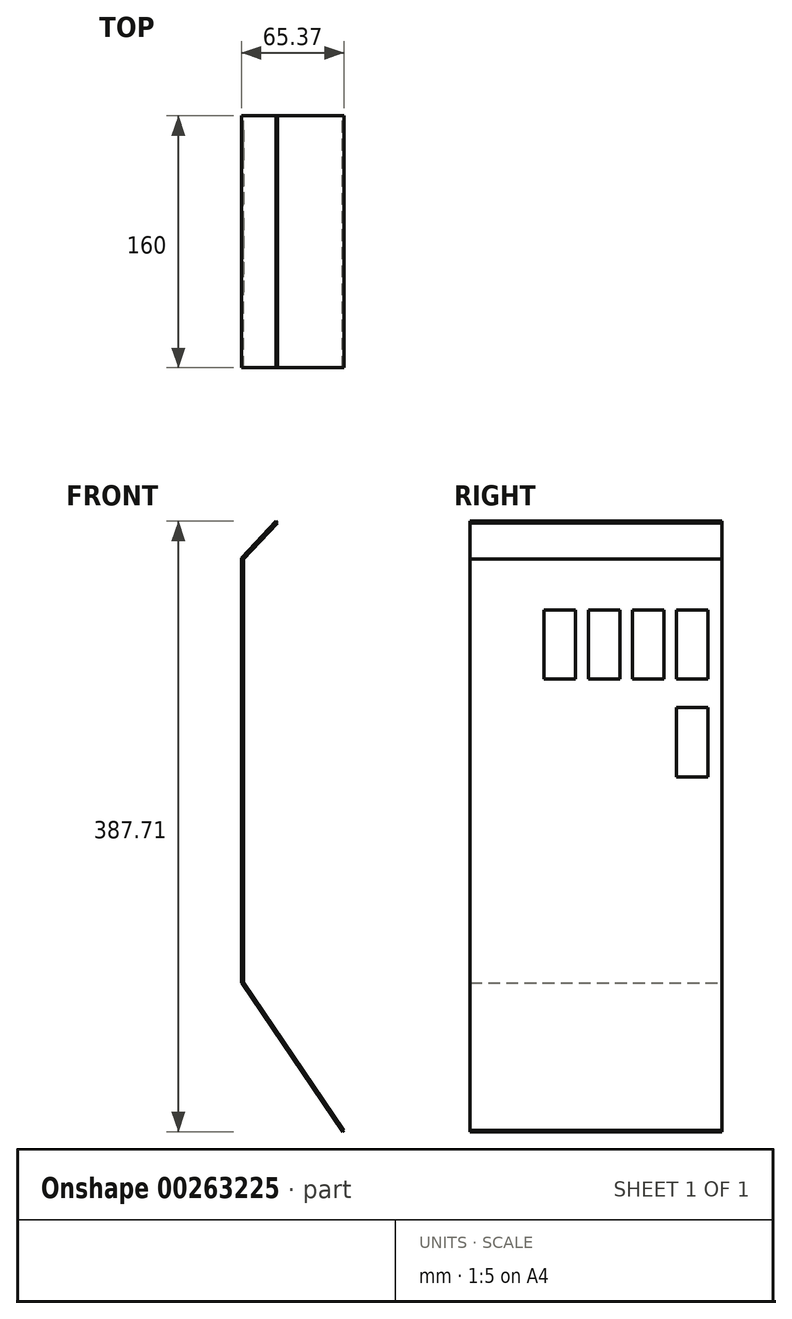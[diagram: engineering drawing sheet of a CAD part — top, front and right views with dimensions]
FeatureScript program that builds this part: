
annotation { "Feature Type Name" : "Feature", "Feature Type Description" : "" }
export const myFeature = defineFeature(function(context is Context, id is Id, definition is map)
    precondition{}
    {
        {
            var Q0;
            Q0=qCreatedBy(makeId("Front.planeOp"),FACE);
            var sketch = newSketch(context, id + "F0", { "sketchPlane" : qUnion([Q0])});
            skLineSegment(sketch, "E0", {"start": v(0, 0) * mm, "end": v(0, 270) * mm});
            skLineSegment(sketch, "E1", {"start": v(64.13, -94.4) * mm, "end": v(0, 0) * mm});
            skLineSegment(sketch, "E2", {"start": v(21.92, 293.3) * mm, "end": v(0, 270) * mm});
            skLineSegment(sketch, "E3.0", {"start": v(23.02, 292.28) * mm, "end": v(1.5, 269.4) * mm});
            skLineSegment(sketch, "E3.1", {"start": v(1.5, 1.08) * mm, "end": v(1.5, 269.4) * mm});
            skLineSegment(sketch, "E3.2", {"start": v(65.37, -93.56) * mm, "end": v(1.85, -0.05) * mm});
            skLineSegment(sketch, "E4", {"start": v(21.92, 293.3) * mm, "end": v(23.02, 292.28) * mm});
            skLineSegment(sketch, "E5", {"start": v(64.13, -94.4) * mm, "end": v(65.37, -93.56) * mm});
            skPoint(sketch, "E6.visualSharp", {"position": v(1.5, 0.46) * mm});
            skArc(sketch, "E6.filletArc", {"start": v(1.5, 1.08) * mm, "mid": v(1.59, 0.49) * mm, "end": v(1.85, -0.05) * mm});
            skSolve(sketch);
        }
        {
            var Q0;
            Q0 = qSketchRegion(id + "F0", true);
            extrude(context, id + "F1", {"entities" : qUnion([Q0]), "depth" : 160 * mm});
        }
        {
            var Q0;
            Q0=makeQuery(id+"F1.opExtrude","SWEPT_FACE",FACE,{"disambiguationData":[OSD([sQuery(id+"F0.wireOp",EDGE,"E0")])]});
            var sketch = newSketch(context, id + "F2", { "sketchPlane" : qUnion([Q0])});
            skLineSegment(sketch, "E7", {"start": v(9, 237) * mm, "end": v(9, 193) * mm});
            skLineSegment(sketch, "E8", {"start": v(9, 193) * mm, "end": v(29, 193) * mm});
            skLineSegment(sketch, "E9", {"start": v(29, 193) * mm, "end": v(29, 237) * mm});
            skLineSegment(sketch, "E10", {"start": v(9, 237) * mm, "end": v(29, 237) * mm});
            skLineSegment(sketch, "E11.1.0.0", {"start": v(57, 193) * mm, "end": v(57, 237) * mm});
            skLineSegment(sketch, "E11.1.0.1", {"start": v(37, 237) * mm, "end": v(37, 193) * mm});
            skLineSegment(sketch, "E11.1.0.2", {"start": v(37, 193) * mm, "end": v(57, 193) * mm});
            skLineSegment(sketch, "E11.1.0.3", {"start": v(37, 237) * mm, "end": v(57, 237) * mm});
            skLineSegment(sketch, "E11.2.0.0", {"start": v(85, 193) * mm, "end": v(85, 237) * mm});
            skLineSegment(sketch, "E11.2.0.1", {"start": v(65, 237) * mm, "end": v(65, 193) * mm});
            skLineSegment(sketch, "E11.2.0.2", {"start": v(65, 193) * mm, "end": v(85, 193) * mm});
            skLineSegment(sketch, "E11.2.0.3", {"start": v(65, 237) * mm, "end": v(85, 237) * mm});
            skLineSegment(sketch, "E11.3.0.0", {"start": v(113, 193) * mm, "end": v(113, 237) * mm});
            skLineSegment(sketch, "E11.3.0.1", {"start": v(93, 237) * mm, "end": v(93, 193) * mm});
            skLineSegment(sketch, "E11.3.0.2", {"start": v(93, 193) * mm, "end": v(113, 193) * mm});
            skLineSegment(sketch, "E11.3.0.3", {"start": v(93, 237) * mm, "end": v(113, 237) * mm});
            skLineSegment(sketch, "E11.direction1", {"start": v(9, 193) * mm, "end": v(37, 193) * mm, "construction": true});
            skLineSegment(sketch, "E12.0.1.0", {"start": v(9, 175) * mm, "end": v(29, 175) * mm});
            skLineSegment(sketch, "E12.0.1.1", {"start": v(9, 175) * mm, "end": v(9, 131) * mm});
            skLineSegment(sketch, "E12.0.1.2", {"start": v(29, 131) * mm, "end": v(29, 175) * mm});
            skLineSegment(sketch, "E12.0.1.3", {"start": v(9, 131) * mm, "end": v(29, 131) * mm});
            skLineSegment(sketch, "E12.direction1", {"start": v(9, 193) * mm, "end": v(34, 193) * mm, "construction": true});
            skLineSegment(sketch, "E12.direction2", {"start": v(9, 193) * mm, "end": v(9, 131) * mm, "construction": true});
            skSolve(sketch);
        }
        {
            var Q0;
            Q0 = qSketchRegion(id + "F2", true);
            extrude(context, id + "F3", {"entities" : qUnion([Q0]), "operationType" : NewBodyOperationType.REMOVE, "endBound" : BoundingType.THROUGH_ALL, "oppositeDirection" : true, "depth" : 25 * mm});
        }
    });
